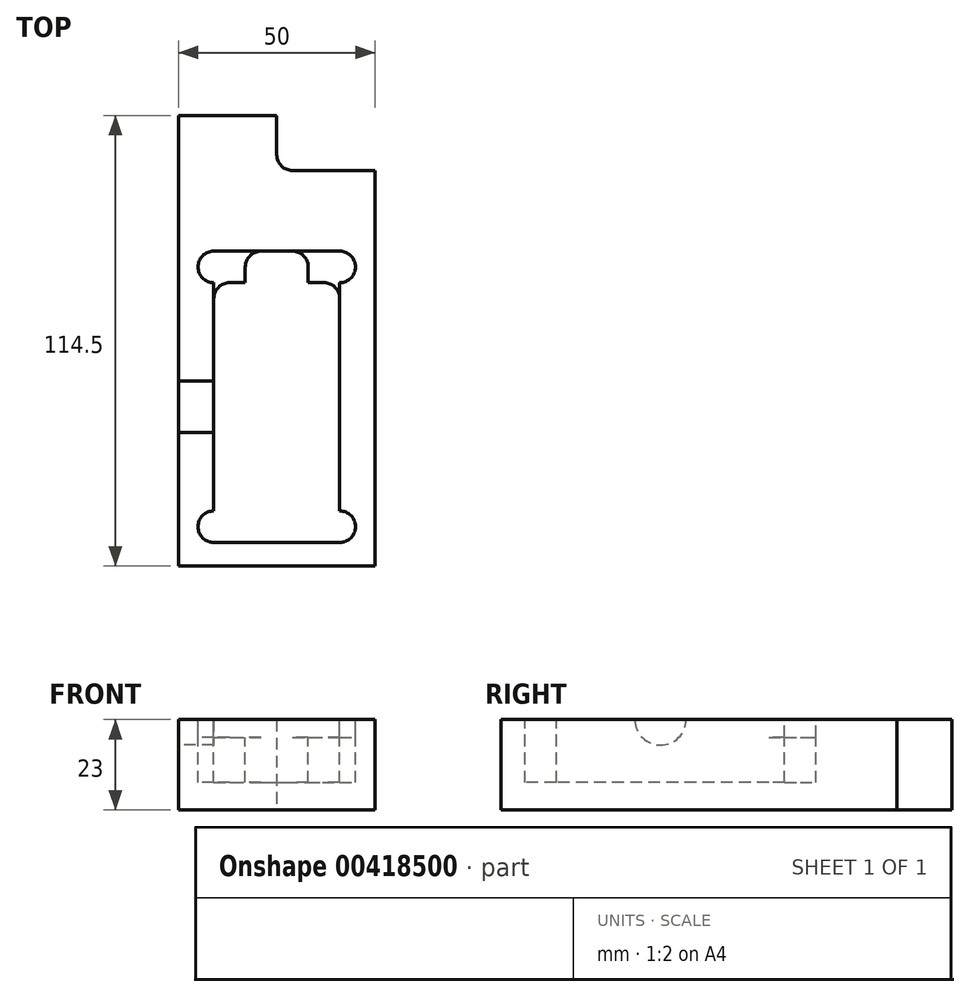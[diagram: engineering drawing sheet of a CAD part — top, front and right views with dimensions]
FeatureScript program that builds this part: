
annotation { "Feature Type Name" : "Feature", "Feature Type Description" : "" }
export const myFeature = defineFeature(function(context is Context, id is Id, definition is map)
    precondition{}
    {
        {
            var Q0;
            Q0=qCreatedBy(makeId("Top.planeOp"),FACE);
            var sketch = newSketch(context, id + "F0", { "sketchPlane" : qUnion([Q0])});
            skLineSegment(sketch, "E0.bottom", {"start": v(0, 0) * mm, "end": v(50, 0) * mm});
            skLineSegment(sketch, "E0.top", {"start": v(0, 114.5) * mm, "end": v(25, 114.5) * mm});
            skLineSegment(sketch, "E0.left", {"start": v(0, 0) * mm, "end": v(0, 114.5) * mm});
            skLineSegment(sketch, "E0.right", {"start": v(50, 0) * mm, "end": v(50, 100.5) * mm});
            skPoint(sketch, "E1.endSnap0", {"position": v(25, 114.5) * mm});
            skLineSegment(sketch, "E2", {"start": v(25, 114.5) * mm, "end": v(25, 104.5) * mm});
            skLineSegment(sketch, "E3", {"start": v(29, 100.5) * mm, "end": v(50, 100.5) * mm});
            skPoint(sketch, "E4.orphan", {"position": v(50, 114.5) * mm});
            skPoint(sketch, "E5.visualSharp", {"position": v(25, 100.5) * mm});
            skArc(sketch, "E5.filletArc", {"start": v(25, 104.5) * mm, "mid": v(26.17, 101.67) * mm, "end": v(29, 100.5) * mm});
            skSolve(sketch);
        }
        {
            var Q0;
            Q0 = qSketchRegion(id + "F0", true);
            extrude(context, id + "F1", {"entities" : qUnion([Q0]), "depth" : 23 * mm});
        }
        {
            var Q0;
            Q0=makeQuery(id+"F1.opExtrude","CAP_FACE",FACE,{"disambiguationData":[OSD([sQuery(id+"F0.wireOp",EDGE,"E0.bottom"),sQuery(id+"F0.wireOp",EDGE,"E0.top"),sQuery(id+"F0.wireOp",EDGE,"E0.left"),sQuery(id+"F0.wireOp",EDGE,"E0.right"),sQuery(id+"F0.wireOp",EDGE,"E2"),sQuery(id+"F0.wireOp",EDGE,"E3")])],"isStart":false});
            var sketch = newSketch(context, id + "F2", { "sketchPlane" : qUnion([Q0])});
            skLineSegment(sketch, "E6.bottom", {"start": v(9, 80) * mm, "end": v(41, 80) * mm});
            skLineSegment(sketch, "E6.right", {"start": v(41, 72) * mm, "end": v(41, 14) * mm});
            skArc(sketch, "E7", {"start": v(9, 80) * mm, "mid": v(5, 76) * mm, "end": v(9, 72) * mm});
            skArc(sketch, "E8", {"start": v(41, 72) * mm, "mid": v(45, 76) * mm, "end": v(41, 80) * mm});
            skLineSegment(sketch, "E9", {"start": v(9, 6) * mm, "end": v(41, 6) * mm});
            skPoint(sketch, "E9.startSnap0", {"position": v(24.8, 6) * mm});
            skArc(sketch, "E10", {"start": v(9, 14) * mm, "mid": v(5, 10) * mm, "end": v(9, 6) * mm});
            skArc(sketch, "E11", {"start": v(41, 6) * mm, "mid": v(45, 10) * mm, "end": v(41, 14) * mm});
            skLineSegment(sketch, "E12.trimOffspring", {"start": v(9, 72) * mm, "end": v(9, 14) * mm});
            skSolve(sketch);
        }
        {
            var Q0;
            Q0 = qSketchRegion(id + "F2", true);
            extrude(context, id + "F3", {"entities" : qUnion([Q0]), "operationType" : NewBodyOperationType.REMOVE, "oppositeDirection" : true, "depth" : 4.5 * mm});
        }
        {
            var Q0;
            Q0=makeQuery(id+"F3.boolean.opBoolean","COPY",FACE,{"derivedFrom":makeQuery(id+"F3.opExtrude","CAP_FACE",FACE,{"disambiguationData":[OSD([sQuery(id+"F2.wireOp",EDGE,"E6.bottom"),sQuery(id+"F2.wireOp",EDGE,"E6.right"),sQuery(id+"F2.wireOp",EDGE,"E7"),sQuery(id+"F2.wireOp",EDGE,"E8"),sQuery(id+"F2.wireOp",EDGE,"E9"),sQuery(id+"F2.wireOp",EDGE,"E10"),sQuery(id+"F2.wireOp",EDGE,"E11"),sQuery(id+"F2.wireOp",EDGE,"E12.trimOffspring")])],"isStart":false})});
            var sketch = newSketch(context, id + "F4", { "sketchPlane" : qUnion([Q0])});
            skLineSegment(sketch, "E13", {"start": v(9, 14) * mm, "end": v(9, 68) * mm});
            skLineSegment(sketch, "E14", {"start": v(13, 72) * mm, "end": v(17, 72) * mm});
            skLineSegment(sketch, "E15", {"start": v(41, 68) * mm, "end": v(41, 14) * mm});
            skLineSegment(sketch, "E16", {"start": v(9, 6) * mm, "end": v(41, 6) * mm});
            skArc(sketch, "E17", {"start": v(41, 6) * mm, "mid": v(45, 10) * mm, "end": v(41, 14) * mm});
            skArc(sketch, "E18", {"start": v(9, 14) * mm, "mid": v(5, 10) * mm, "end": v(9, 6) * mm});
            skPoint(sketch, "E19.visualSharp", {"position": v(9, 72) * mm});
            skArc(sketch, "E19.filletArc", {"start": v(13, 72) * mm, "mid": v(10.17, 70.83) * mm, "end": v(9, 68) * mm});
            skPoint(sketch, "E20.visualSharp", {"position": v(41, 72) * mm});
            skArc(sketch, "E20.filletArc", {"start": v(41, 68) * mm, "mid": v(39.83, 70.83) * mm, "end": v(37, 72) * mm});
            skLineSegment(sketch, "E21.top", {"start": v(21, 80) * mm, "end": v(29, 80) * mm});
            skLineSegment(sketch, "E21.left", {"start": v(17, 72) * mm, "end": v(17, 76) * mm});
            skLineSegment(sketch, "E21.right", {"start": v(33, 72) * mm, "end": v(33, 76) * mm});
            skLineSegment(sketch, "E22.trimOffspring", {"start": v(33, 72) * mm, "end": v(37, 72) * mm});
            skPoint(sketch, "E23.visualSharp", {"position": v(17, 80) * mm});
            skArc(sketch, "E23.filletArc", {"start": v(21, 80) * mm, "mid": v(18.17, 78.83) * mm, "end": v(17, 76) * mm});
            skPoint(sketch, "E24.visualSharp", {"position": v(33, 80) * mm});
            skArc(sketch, "E24.filletArc", {"start": v(33, 76) * mm, "mid": v(31.83, 78.83) * mm, "end": v(29, 80) * mm});
            skSolve(sketch);
        }
        {
            var Q0;
            Q0=makeQuery(id+"F4.imprint","IMPRINT",FACE,{"disambiguationData":[TD([[makeQuery(id+"F4.imprint","IMPRINT",EDGE,{"derivedFrom":sQuery(id+"F4.wireOp",EDGE,"E13")}),1.0]])]});
            extrude(context, id + "F5", {"entities" : qUnion([Q0]), "operationType" : NewBodyOperationType.REMOVE, "oppositeDirection" : true, "depth" : 11.5 * mm});
        }
        {
            var Q0;
            Q0=makeQuery(id+"F1.opExtrude","SWEPT_FACE",FACE,{"disambiguationData":[OSD([sQuery(id+"F0.wireOp",EDGE,"E0.left")])]});
            var sketch = newSketch(context, id + "F6", { "sketchPlane" : qUnion([Q0])});
            skCircle(sketch, "E25", {"center": v(-40.5, 23) * mm, "radius": 6.5 * mm});
            skLineSegment(sketch, "E26", {"start": v(5, 45.4) * mm, "end": v(5, 44.47) * mm});
            skSolve(sketch);
        }
        {
            var Q0;
            Q0 = qSketchRegion(id + "F6", true);
            var Q1;
            Q1=makeQuery(id+"F3.boolean.opBoolean","COPY",FACE,{"derivedFrom":makeQuery(id+"F3.opExtrude","SWEPT_FACE",FACE,{"disambiguationData":[OSD([sQuery(id+"F2.wireOp",EDGE,"E12.trimOffspring")])]})});
            extrude(context, id + "F7", {"entities" : qUnion([Q0]), "operationType" : NewBodyOperationType.REMOVE, "endBound" : BoundingType.UP_TO_SURFACE, "oppositeDirection" : true, "endBoundEntityFace" : qUnion([Q1]), "depth" : 25 * mm});
        }
    });
